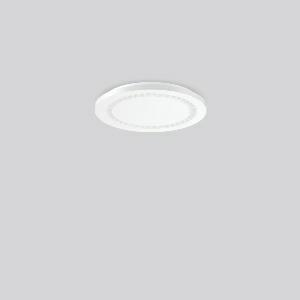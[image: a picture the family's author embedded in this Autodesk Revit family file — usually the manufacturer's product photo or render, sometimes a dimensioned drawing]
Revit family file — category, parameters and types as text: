
# Revit family: hemis_round_312185_002_2_ec4a
name_source: partatom
category: Lighting Fixtures
units: mm (PartAtom-declared; Revit-internal decimal feet)

## family parameters
Cut with Voids When Loaded = No
Host = Face
Light Source = No
Part Type = Normal
Room Calculation Point = No
Round Connector Dimension = Use Diameter
Shared = No

## types (1)
- MultiLumen 1 (1 x LED Modul 830, 1850 lm, 3000)
    Apparent Load = 16 VA
    CIE Flux Codes = 87 99 100 100 100
    Color Rendering = 80
    Color Temperature = 3000
    Default Elevation = 1800 mm
    Description = Series: HEMIS round
Glare-free LED ceiling luminaire with optical lens system. Base: metal, powder-coated, with bayonet fixing. Housing: plastic (polycarbonate). Housing and diffuser are screwed together. Diffuser with optic lenses. Big terminal block; ideal for through-wiring. Sealing strip on the back of the luminaire connects seamlessly with the ceiling. Easy installation with Plug+Play plug connection. Thanks to RUG < 22 ideal for corridors, stairways, shops, schools, meeting rooms, rest areas. 
Colour: white
Diameter: 300 mm
Height: 33 mm
Lamp: LED
Socket: without socket
Colour temperature: 3000K
Colour rendering index (CRI): 80
System power: 16 W
Rated luminous flux: 1850 lm
Luminous efficiency: 116 lm/W
System power 2: 10 W
Rated luminous flux 2: 1200 lm
Luminous efficiency 2: 120 lm/W
Control gear: Regulated power supply
Protection class: I
Type of protection: IP 40
    Height = 33 mm
    Lamp = 1 x LED Modul 830
    Lamp Light Flux = 1850 lm
    Lamp count = 1
    Length = 300 mm
    Lifetime = 50000 h
    Luminous efficacy = 116 lm/W
    Manufacturer = RZB
    ModVariant = No
    Model = 312185.002.2
    Mounting Place = Ceiling
    Mounting Type = Surface mounted
    Number of Poles = 1
    OnlyDefault = Yes
    Power Factor = 1
    Product Name = HEMIS round
    Product group = Surface mounted modular luminaires
    ProductGroupID = 306
    Protection Class = Protection class I
    Protection Degree = Degree of protection
    RLX_Detail_Level = 1
    RLX_Emergency_Light_Flux = 0 lm
    RLX_Emergency_Type = 0
    RLX_Emergency_Type_DB = No
    RlxData = <blob elided: 40817 chars, md5=e3fb9b07>
    Socket = socket
    Standby Power = 0 W
    System Light Flux = 1850 lm
    System Power = 16 W
    Type Comments = MultiLumen 1
    Type Image = 312185.002.jpg
    URL = http://relux.com
    VarID = multilumen_1
    Voltage = 0 V
    Weight = 0.00 kg
    Width = 0 mm  [stored 0 ft]

note: [stored X ft] marks values corroborated as IEEE doubles in the binary element streams (Revit-internal decimal feet)

## geometry (parser evidence)
native form markers: Blend x4, Sweep x9
no freeform markers — native parametric forms only
